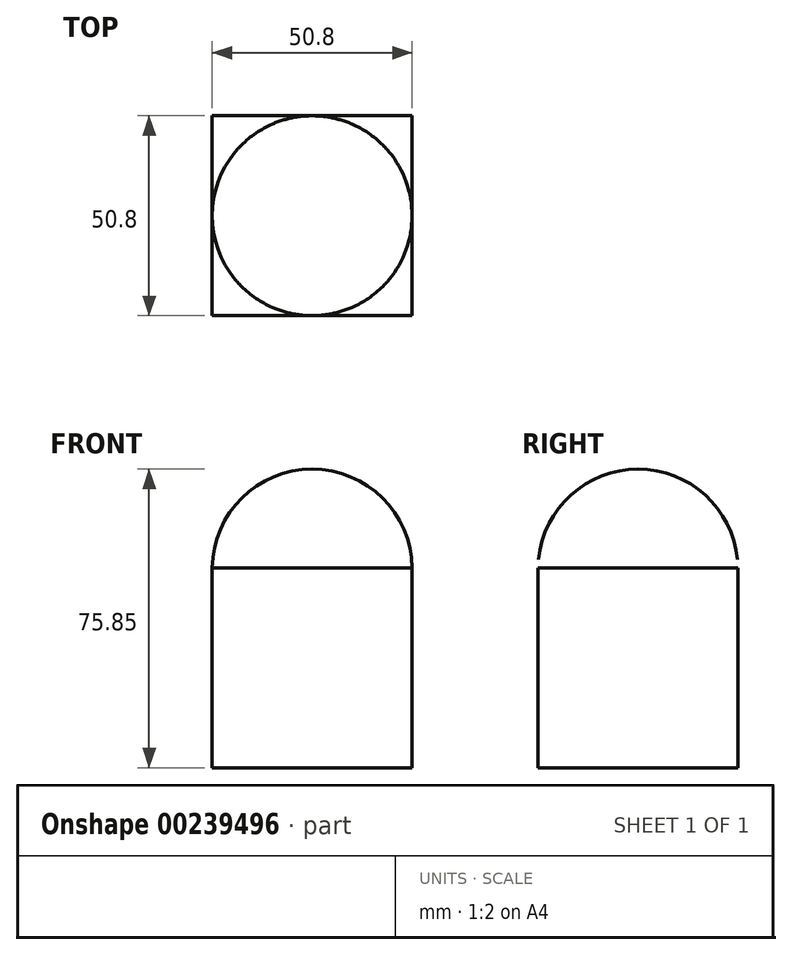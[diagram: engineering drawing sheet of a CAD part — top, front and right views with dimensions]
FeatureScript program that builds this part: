
annotation { "Feature Type Name" : "Feature", "Feature Type Description" : "" }
export const myFeature = defineFeature(function(context is Context, id is Id, definition is map)
    precondition{}
    {
        {
            var Q0;
            Q0=qCreatedBy(makeId("Top.planeOp"),FACE);
            var sketch = newSketch(context, id + "F0", { "sketchPlane" : qUnion([Q0])});
            skLineSegment(sketch, "E0.bottom", {"start": v(25.4, 25.4) * mm, "end": v(-25.4, 25.4) * mm});
            skLineSegment(sketch, "E0.top", {"start": v(25.4, -25.4) * mm, "end": v(-25.4, -25.4) * mm});
            skLineSegment(sketch, "E0.left", {"start": v(25.4, 25.4) * mm, "end": v(25.4, -25.4) * mm});
            skLineSegment(sketch, "E0.right", {"start": v(-25.4, 25.4) * mm, "end": v(-25.4, -25.4) * mm});
            skPoint(sketch, "E0.middle", {"position": v(0, 0) * mm});
            skSolve(sketch);
        }
        {
            var Q0;
            Q0 = qSketchRegion(id + "F0", true);
            extrude(context, id + "F1", {"entities" : qUnion([Q0]), "depth" : 50.8 * mm});
        }
        {
            var Q0;
            Q0=qCreatedBy(makeId("Right.planeOp"),FACE);
            var sketch = newSketch(context, id + "F2", { "sketchPlane" : qUnion([Q0])});
            skArc(sketch, "E1", {"start": v(25.4, 50.45) * mm, "mid": v(0, 75.85) * mm, "end": v(-25.4, 50.45) * mm});
            skLineSegment(sketch, "E2", {"start": v(-25.4, 50.45) * mm, "end": v(25.4, 50.45) * mm});
            skSolve(sketch);
        }
        {
            var Q0;
            Q0 = qSketchRegion(id + "F2", true);
            var Q1;
            Q1=sQuery(id+"F2.wireOp",EDGE,"E2");
            revolve(context, id + "F3", {"operationType" : NewBodyOperationType.ADD, "entities" : qUnion([Q0]), "axis" : qUnion([Q1]), "revolveType" : RevolveType.FULL});
        }
    });
